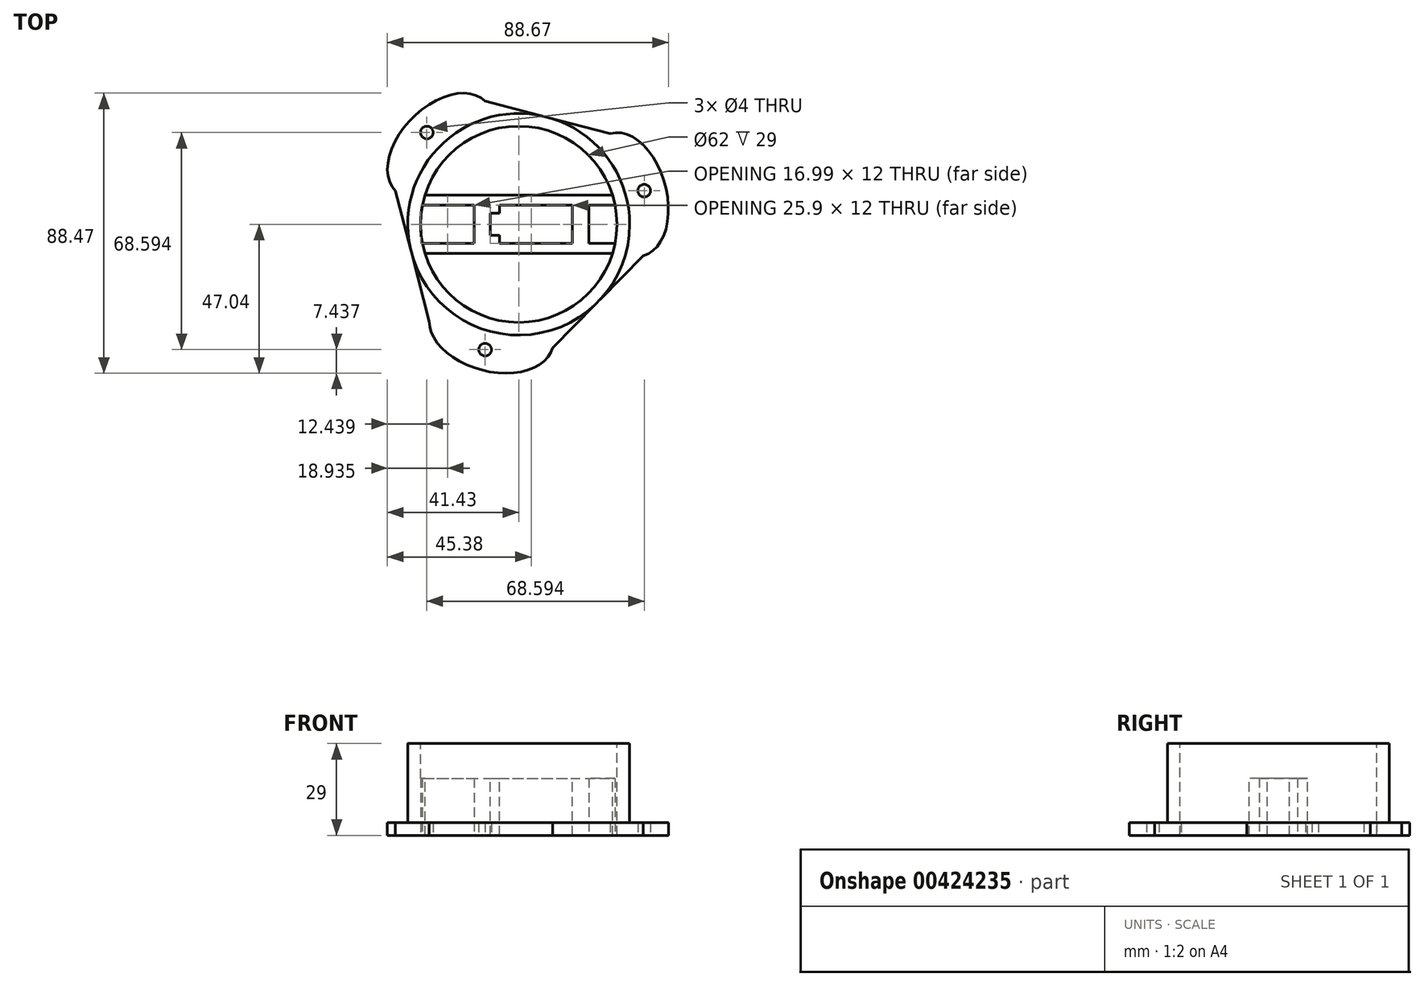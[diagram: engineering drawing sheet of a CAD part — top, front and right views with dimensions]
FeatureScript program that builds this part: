
annotation { "Feature Type Name" : "Feature", "Feature Type Description" : "" }
export const myFeature = defineFeature(function(context is Context, id is Id, definition is map)
    precondition{}
    {
        {
            var Q0;
            Q0=qCreatedBy(makeId("Top.planeOp"),FACE);
            var sketch = newSketch(context, id + "F0", { "sketchPlane" : qUnion([Q0])});
            skCircle(sketch, "E0", {"center": v(0, 0) * mm, "radius": 35 * mm, "construction": true});
            skLineSegment(sketch, "E1", {"start": v(0, 0) * mm, "end": v(-53.68, 53.68) * mm, "construction": true});
            skLineSegment(sketch, "E2", {"start": v(-24.75, 24.75) * mm, "end": v(-10.6, 38.9) * mm, "construction": true});
            skPoint(sketch, "E2.endSnap0", {"position": v(-10.6, 38.9) * mm});
            skPoint(sketch, "E3.center", {"position": v(0.24, 0.08) * mm});
            skLineSegment(sketch, "E4", {"start": v(-10.6, 38.9) * mm, "end": v(28.93, 28.7) * mm});
            skLineSegment(sketch, "E5", {"start": v(39.28, -9.93) * mm, "end": v(10.7, -39.08) * mm});
            skLineSegment(sketch, "E6", {"start": v(-38.9, 10.6) * mm, "end": v(-28.21, -30.72) * mm});
            skLineSegment(sketch, "E7", {"start": v(10.7, -39.08) * mm, "end": v(-8.62, -33.9) * mm, "construction": true});
            skEllipticalArc(sketch, "E8", {});
            skEllipticalArc(sketch, "E9", {"construction": true});
            skEllipticalArc(sketch, "E10", {"construction": true});
            skEllipticalArc(sketch, "E11", {});
            skEllipticalArc(sketch, "E12", {});
            skEllipticalArc(sketch, "E13", {"construction": true});
            skCircle(sketch, "E14", {"center": v(-29, 29) * mm, "radius": 2 * mm});
            skCircle(sketch, "E15.1.0", {"center": v(-10.61, -39.6) * mm, "radius": 2 * mm});
            skCircle(sketch, "E15.2.0", {"center": v(39.6, 10.61) * mm, "radius": 2 * mm});
            const initialGuessF0  = {"E8": [-0.024748737341529173, 0.02474873734152916, 0.7071067811865474, 0.7071067811865478, 0.02, 0.0125, 0, 3.141592653589793], "E9": [-0.024748737341529173, 0.02474873734152916, 0.7071067811865474, 0.7071067811865478, 0.02, 0.0125, 3.141592653589793, 0], "E10": [0.03410784128529934, 0.00938656512054002, 0.2588190451025208, -0.9659258262890683, 0.02, 0.0125, 3.141592653589793, 0], "E11": [0.03410784128529934, 0.00938656512054002, 0.2588190451025208, -0.9659258262890683, 0.02, 0.0125, 0, 3.141592653589793], "E12": [-0.008624479428803128, -0.0339036410396351, -0.9659258262890682, 0.25881904510252096, 0.02, 0.0125, 0.16001835229444727, 3.141592653589793], "E13": [-0.008624479428803128, -0.0339036410396351, -0.9659258262890682, 0.25881904510252096, 0.02, 0.0125, 3.141592653589793, 0.16001835229444727]};
            skSetInitialGuess(sketch, initialGuessF0);
            skSolve(sketch);
        }
        {
            var Q0;
            Q0=makeQuery(id+"F0.imprint","IMPRINT",FACE,{"disambiguationData":[TD([[makeQuery(id+"F0.imprint","IMPRINT",EDGE,{"derivedFrom":sQuery(id+"F0.wireOp",EDGE,"E4")}),-1.0]])]});
            var Q1;
            Q1=sQuery(id+"F0.wireOp",EDGE,"E4");
            var Q2;
            Q2=sQuery(id+"F0.wireOp",EDGE,"E8");
            var Q3;
            Q3=sQuery(id+"F0.wireOp",EDGE,"E6");
            var Q4;
            Q4=sQuery(id+"F0.wireOp",EDGE,"E12");
            var Q5;
            Q5=sQuery(id+"F0.wireOp",EDGE,"E5");
            var Q6;
            Q6=sQuery(id+"F0.wireOp",EDGE,"E11");
            extrude(context, id + "F1", {"entities" : qUnion([Q0]), "surfaceEntities" : qUnion([Q1, Q2, Q3, Q4, Q5, Q6]), "depth" : 4 * mm});
        }
        {
            var Q0;
            Q0=makeQuery(id+"F1.opExtrude","CAP_FACE",FACE,{"disambiguationData":[OSD([sQuery(id+"F0.wireOp",EDGE,"E4"),sQuery(id+"F0.wireOp",EDGE,"E5"),sQuery(id+"F0.wireOp",EDGE,"E6"),sQuery(id+"F0.wireOp",EDGE,"E8"),sQuery(id+"F0.wireOp",EDGE,"E11"),sQuery(id+"F0.wireOp",EDGE,"E12")])],"isStart":false});
            var sketch = newSketch(context, id + "F2", { "sketchPlane" : qUnion([Q0])});
            skCircle(sketch, "E16", {"center": v(0, 0) * mm, "radius": 35.02 * mm});
            skSolve(sketch);
        }
        {
            var Q0;
            Q0=qSketchRegion(id+"F2",true);
            extrude(context, id + "F3", {"entities" : qUnion([Q0]), "operationType" : NewBodyOperationType.ADD, "depth" : 25 * mm});
        }
        {
            var Q0;
            Q0=makeQuery(id+"F3.opExtrude","CAP_FACE",FACE,{"disambiguationData":[OSD([sQuery(id+"F2.wireOp",EDGE,"E16")])],"isStart":false});
            var sketch = newSketch(context, id + "F4", { "sketchPlane" : qUnion([Q0])});
            skCircle(sketch, "E17", {"center": v(0, 0) * mm, "radius": 31 * mm});
            skSolve(sketch);
        }
        {
            var Q0;
            Q0=makeQuery(id+"F4.imprint","IMPRINT",FACE,{"disambiguationData":[TD([[makeQuery(id+"F4.imprint","IMPRINT",EDGE,{"derivedFrom":sQuery(id+"F4.wireOp",EDGE,"E17")}),1.0]])]});
            extrude(context, id + "F5", {"entities" : qUnion([Q0]), "operationType" : NewBodyOperationType.REMOVE, "endBound" : BoundingType.THROUGH_ALL, "oppositeDirection" : true, "depth" : 25 * mm});
        }
        {
            var Q0;
            Q0=qCreatedBy(makeId("Top.planeOp"),FACE);
            var sketch = newSketch(context, id + "F6", { "sketchPlane" : qUnion([Q0])});
            skLineSegment(sketch, "E18.bottom", {"start": v(-31.5, 9.25) * mm, "end": v(31.5, 9.25) * mm});
            skLineSegment(sketch, "E18.top", {"start": v(-31.5, -9.25) * mm, "end": v(31.5, -9.25) * mm});
            skLineSegment(sketch, "E18.left", {"start": v(-31.5, 9.25) * mm, "end": v(-31.5, -9.25) * mm});
            skLineSegment(sketch, "E18.right", {"start": v(31.5, 9.25) * mm, "end": v(31.5, -9.25) * mm});
            skPoint(sketch, "E18.middle", {"position": v(0, 0) * mm});
            skSolve(sketch);
        }
        {
            var Q0;
            Q0=makeQuery(id+"F6.imprint","IMPRINT",FACE,{"disambiguationData":[TD([[makeQuery(id+"F6.imprint","IMPRINT",EDGE,{"derivedFrom":sQuery(id+"F6.wireOp",EDGE,"E18.bottom")}),-1.0]])]});
            extrude(context, id + "F7", {"entities" : qUnion([Q0]), "operationType" : NewBodyOperationType.ADD, "depth" : 18 * mm});
        }
        {
            var Q0;
            Q0=qCreatedBy(makeId("Top.planeOp"),FACE);
            var sketch = newSketch(context, id + "F8", { "sketchPlane" : qUnion([Q0])});
            skLineSegment(sketch, "E19.bottom", {"start": v(31.5, 9.25) * mm, "end": v(-31.5, 9.25) * mm});
            skLineSegment(sketch, "E19.top", {"start": v(31.5, -9.25) * mm, "end": v(-31.5, -9.25) * mm});
            skLineSegment(sketch, "E19.left", {"start": v(31.5, 9.25) * mm, "end": v(31.5, -9.25) * mm, "construction": true});
            skLineSegment(sketch, "E19.right", {"start": v(-31.5, 9.25) * mm, "end": v(-31.5, -9.25) * mm, "construction": true});
            skPoint(sketch, "E19.middle", {"position": v(0, 0) * mm});
            skLineSegment(sketch, "E20.bottom", {"start": v(-14, 6) * mm, "end": v(-30.4, 6) * mm});
            skLineSegment(sketch, "E20.top", {"start": v(-14, -6) * mm, "end": v(-32, -6) * mm});
            skLineSegment(sketch, "E20.left", {"start": v(-14, 6) * mm, "end": v(-14, -6) * mm});
            skPoint(sketch, "E20.middle", {"position": v(-23, 0) * mm});
            skLineSegment(sketch, "E21.bottom", {"start": v(16.7, 6) * mm, "end": v(-7, 6) * mm});
            skLineSegment(sketch, "E21.top", {"start": v(16.7, -6) * mm, "end": v(-7, -6) * mm});
            skLineSegment(sketch, "E21.left", {"start": v(16.7, 6) * mm, "end": v(16.7, -6) * mm});
            skLineSegment(sketch, "E21.right", {"start": v(-7, 6) * mm, "end": v(-7, 3.5) * mm});
            skPoint(sketch, "E21.middle", {"position": v(4.85, 0) * mm});
            skLineSegment(sketch, "E22.bottom", {"start": v(-7, 3.5) * mm, "end": v(-10, 3.5) * mm});
            skLineSegment(sketch, "E22.top", {"start": v(-7, -3.5) * mm, "end": v(-10, -3.5) * mm});
            skLineSegment(sketch, "E22.left", {"start": v(-7, 3.5) * mm, "end": v(-7, -3.5) * mm, "construction": true});
            skLineSegment(sketch, "E22.right", {"start": v(-10, 3.5) * mm, "end": v(-10, -3.5) * mm});
            skPoint(sketch, "E22.middle", {"position": v(-8.5, 0) * mm});
            skPoint(sketch, "E22.middle.positionSnap0", {"position": v(-7, 0) * mm});
            skPoint(sketch, "E22.centerSnap0", {"position": v(-7, 0) * mm});
            skLineSegment(sketch, "E23", {"start": v(-7, -3.5) * mm, "end": v(-7, -6) * mm});
            skLineSegment(sketch, "E24.bottom", {"start": v(22.2, 6) * mm, "end": v(30.41, 6) * mm});
            skLineSegment(sketch, "E24.top", {"start": v(22.2, -6) * mm, "end": v(32.33, -6) * mm});
            skLineSegment(sketch, "E24.left", {"start": v(22.2, 6) * mm, "end": v(22.2, -6) * mm});
            skLineSegment(sketch, "E24.right", {"start": v(32.33, 6) * mm, "end": v(32.33, -6) * mm, "construction": true});
            skPoint(sketch, "E24.middle", {"position": v(27.27, 0) * mm});
            skLineSegment(sketch, "E25", {"start": v(30.41, 6) * mm, "end": v(32.33, 6) * mm, "construction": true});
            skArc(sketch, "E26", {"start": v(30.41, -6) * mm, "mid": v(31, 0) * mm, "end": v(30.41, 6) * mm});
            skLineSegment(sketch, "E27", {"start": v(-31.5, 6) * mm, "end": v(-32, 6) * mm});
            skArc(sketch, "E28", {"start": v(-30.41, -6) * mm, "mid": v(-30.04, -7.64) * mm, "end": v(-29.59, -9.25) * mm});
            skArc(sketch, "E29", {"start": v(-30.4, 6) * mm, "mid": v(-31, 0) * mm, "end": v(-30.41, -6) * mm});
            skArc(sketch, "E30.trimOffspring", {"start": v(-29.59, 9.25) * mm, "mid": v(-30.03, 7.64) * mm, "end": v(-30.4, 6) * mm});
            skArc(sketch, "E31.trimOffspring", {"start": v(29.59, -9.25) * mm, "mid": v(30.04, -7.64) * mm, "end": v(30.41, -6) * mm});
            skSolve(sketch);
        }
        {
            var Q0;
            Q0=qSketchRegion(id+"F8",true);
            extrude(context, id + "F9", {"entities" : qUnion([Q0]), "operationType" : NewBodyOperationType.REMOVE, "endBound" : BoundingType.THROUGH_ALL, "depth" : 25 * mm});
        }
        {
            var Q0;
            Q0=makeQuery(id+"F7.opExtrude","CAP_FACE",FACE,{"disambiguationData":[OSD([sQuery(id+"F6.wireOp",EDGE,"E18.bottom"),sQuery(id+"F6.wireOp",EDGE,"E18.top"),sQuery(id+"F6.wireOp",EDGE,"E18.left"),sQuery(id+"F6.wireOp",EDGE,"E18.right")])],"isStart":false});
            var sketch = newSketch(context, id + "F10", { "sketchPlane" : qUnion([Q0])});
            skLineSegment(sketch, "E32", {"start": v(-7, 6) * mm, "end": v(-7, 3.5) * mm});
            skLineSegment(sketch, "E33", {"start": v(-9, 3.5) * mm, "end": v(-10, 3.5) * mm});
            skLineSegment(sketch, "E34", {"start": v(-10, 3.5) * mm, "end": v(-10, -3.5) * mm});
            skLineSegment(sketch, "E35", {"start": v(-10, -3.5) * mm, "end": v(-9, -3.5) * mm});
            skLineSegment(sketch, "E36", {"start": v(-7, -3.5) * mm, "end": v(-7, -6) * mm});
            skLineSegment(sketch, "E37.0", {"start": v(-6, 6) * mm, "end": v(-6, 3.5) * mm});
            skLineSegment(sketch, "E38.0", {"start": v(-9, 3.5) * mm, "end": v(-9, -3.5) * mm});
            skLineSegment(sketch, "E39.0", {"start": v(-6, -3.5) * mm, "end": v(-6, -6) * mm});
            skLineSegment(sketch, "E40", {"start": v(-7, -3.5) * mm, "end": v(-6, -3.5) * mm});
            skLineSegment(sketch, "E41", {"start": v(-7, -6) * mm, "end": v(-6, -6) * mm});
            skLineSegment(sketch, "E42", {"start": v(-7, 6) * mm, "end": v(-6, 6) * mm});
            skLineSegment(sketch, "E43", {"start": v(-7, 3.5) * mm, "end": v(-6, 3.5) * mm});
            skSolve(sketch);
        }
        {
            var Q0;
            Q0 = qSketchRegion(id + "F10", true);
            var Q1;
            Q1=makeQuery(id+"F7.boolean.opBoolean","MERGE",FACE,{"derivedFrom":[makeQuery(id+"F1.opExtrude","CAP_FACE",FACE,{"disambiguationData":[OSD([sQuery(id+"F0.wireOp",EDGE,"E4"),sQuery(id+"F0.wireOp",EDGE,"E5"),sQuery(id+"F0.wireOp",EDGE,"E6"),sQuery(id+"F0.wireOp",EDGE,"E8"),sQuery(id+"F0.wireOp",EDGE,"E11"),sQuery(id+"F0.wireOp",EDGE,"E12"),sQuery(id+"F0.wireOp",EDGE,"E14"),sQuery(id+"F0.wireOp",EDGE,"E15.1.0"),sQuery(id+"F0.wireOp",EDGE,"E15.2.0")])],"isStart":true}),makeQuery(id+"F7.opExtrude","CAP_FACE",FACE,{"disambiguationData":[OSD([sQuery(id+"F6.wireOp",EDGE,"E18.bottom"),sQuery(id+"F6.wireOp",EDGE,"E18.top"),sQuery(id+"F6.wireOp",EDGE,"E18.left"),sQuery(id+"F6.wireOp",EDGE,"E18.right")])],"isStart":true})]});
            extrude(context, id + "F11", {"entities" : qUnion([Q0]), "operationType" : NewBodyOperationType.ADD, "endBound" : BoundingType.UP_TO_SURFACE, "oppositeDirection" : true, "endBoundEntityFace" : qUnion([Q1]), "depth" : 25 * mm});
        }
        {
            var Q0;
            Q0=makeQuery(id+"F11.boolean.opBoolean","MERGE",FACE,{"derivedFrom":[makeQuery(id+"F7.opExtrude","CAP_FACE",FACE,{"disambiguationData":[OSD([sQuery(id+"F6.wireOp",EDGE,"E18.bottom"),sQuery(id+"F6.wireOp",EDGE,"E18.top"),sQuery(id+"F6.wireOp",EDGE,"E18.left"),sQuery(id+"F6.wireOp",EDGE,"E18.right")])],"isStart":false}),makeQuery(id+"F11.opExtrude","CAP_FACE",FACE,{"disambiguationData":[OSD([sQuery(id+"F10.wireOp",EDGE,"E32"),sQuery(id+"F10.wireOp",EDGE,"E37.0"),sQuery(id+"F10.wireOp",EDGE,"E42"),sQuery(id+"F10.wireOp",EDGE,"E43")])],"isStart":true}),makeQuery(id+"F11.opExtrude","CAP_FACE",FACE,{"disambiguationData":[OSD([sQuery(id+"F10.wireOp",EDGE,"E33"),sQuery(id+"F10.wireOp",EDGE,"E34"),sQuery(id+"F10.wireOp",EDGE,"E35"),sQuery(id+"F10.wireOp",EDGE,"E38.0")])],"isStart":true}),makeQuery(id+"F11.opExtrude","CAP_FACE",FACE,{"disambiguationData":[OSD([sQuery(id+"F10.wireOp",EDGE,"E36"),sQuery(id+"F10.wireOp",EDGE,"E39.0"),sQuery(id+"F10.wireOp",EDGE,"E40"),sQuery(id+"F10.wireOp",EDGE,"E41")])],"isStart":true})]});
            var sketch = newSketch(context, id + "F12", { "sketchPlane" : qUnion([Q0])});
            skLineSegment(sketch, "E44.0", {"start": v(16.7, -6) * mm, "end": v(16.7, 6) * mm});
            skLineSegment(sketch, "E45.0", {"start": v(16.9, -6) * mm, "end": v(16.9, 6) * mm});
            skLineSegment(sketch, "E46", {"start": v(16.7, 6) * mm, "end": v(16.9, 6) * mm});
            skLineSegment(sketch, "E47", {"start": v(16.7, -6) * mm, "end": v(16.9, -6) * mm});
            skSolve(sketch);
        }
        {
            var Q0;
            Q0 = qSketchRegion(id + "F12", true);
            extrude(context, id + "F13", {"entities" : qUnion([Q0]), "operationType" : NewBodyOperationType.REMOVE, "endBound" : BoundingType.THROUGH_ALL, "oppositeDirection" : true, "depth" : 25 * mm});
        }
    });
